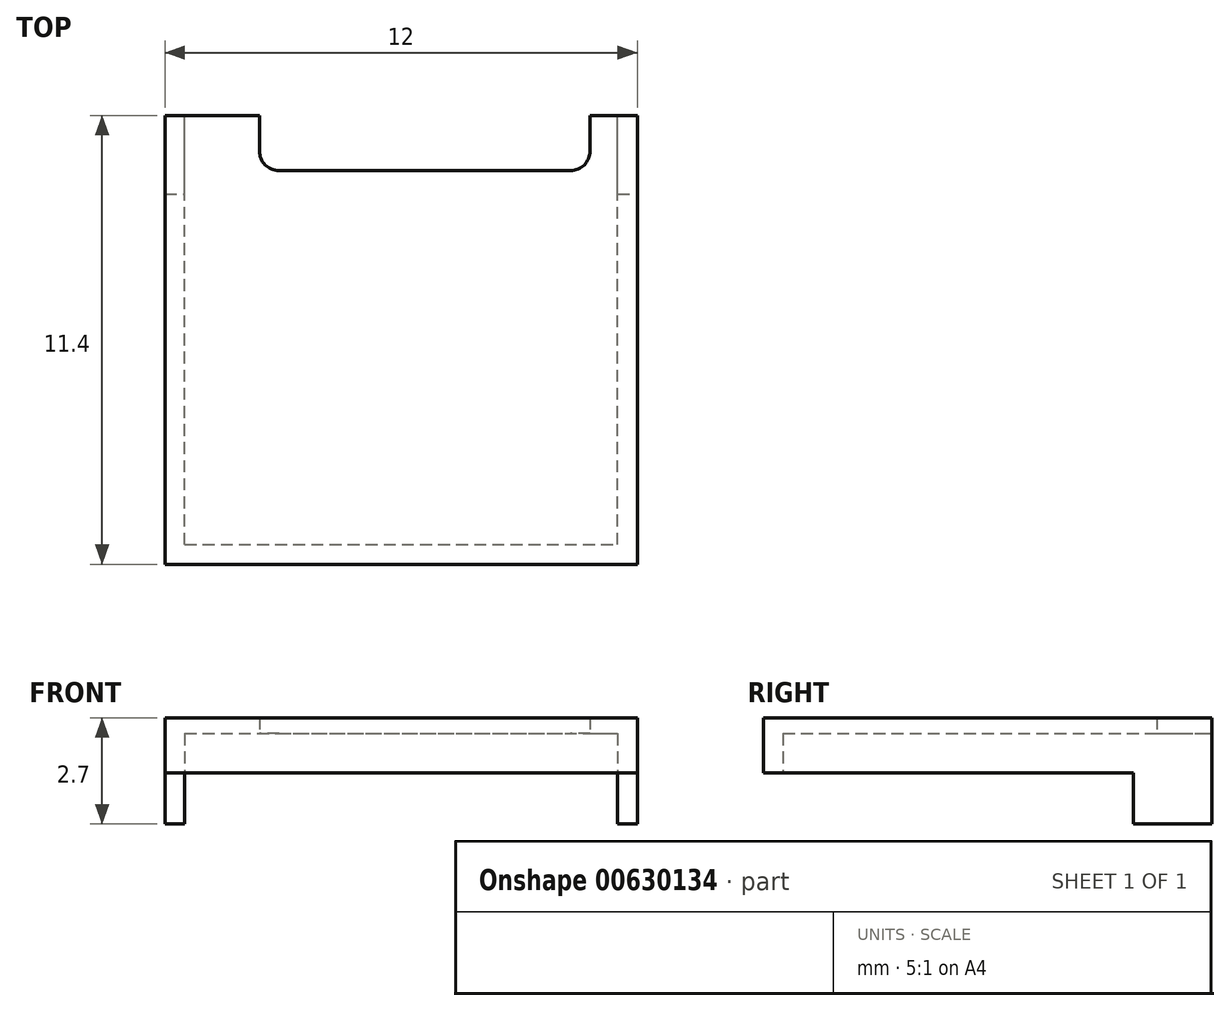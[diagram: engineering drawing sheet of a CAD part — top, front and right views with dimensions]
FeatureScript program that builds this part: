
annotation { "Feature Type Name" : "Feature", "Feature Type Description" : "" }
export const myFeature = defineFeature(function(context is Context, id is Id, definition is map)
    precondition{}
    {
        {
            var Q0;
            Q0=qCreatedBy(makeId("Top.planeOp"),FACE);
            var sketch = newSketch(context, id + "F0", { "sketchPlane" : qUnion([Q0])});
            skLineSegment(sketch, "E0.bottom", {"start": v(0, 0) * mm, "end": v(12, 0) * mm});
            skLineSegment(sketch, "E0.top", {"start": v(0, 11.4) * mm, "end": v(2.4, 11.4) * mm});
            skLineSegment(sketch, "E0.left", {"start": v(0, 0) * mm, "end": v(0, 11.4) * mm});
            skLineSegment(sketch, "E0.right", {"start": v(12, 0) * mm, "end": v(12, 11.4) * mm});
            skLineSegment(sketch, "E1", {"start": v(2.4, 11.4) * mm, "end": v(2.4, 10) * mm});
            skLineSegment(sketch, "E2", {"start": v(2.4, 10) * mm, "end": v(10.8, 10) * mm});
            skLineSegment(sketch, "E3", {"start": v(10.8, 10) * mm, "end": v(10.8, 11.4) * mm});
            skLineSegment(sketch, "E4.trimOffspring", {"start": v(10.8, 11.4) * mm, "end": v(12, 11.4) * mm});
            skSolve(sketch);
        }
        {
            var Q0;
            Q0=qSketchRegion(id+"F0",true);
            extrude(context, id + "F1", {"entities" : qUnion([Q0]), "depth" : 1.4 * mm});
        }
        {
            var Q0;
            Q0=makeQuery(id+"F1.opExtrude","CAP_FACE",FACE,{"disambiguationData":[OSD([sQuery(id+"F0.wireOp",EDGE,"E0.bottom"),sQuery(id+"F0.wireOp",EDGE,"E0.top"),sQuery(id+"F0.wireOp",EDGE,"E0.left"),sQuery(id+"F0.wireOp",EDGE,"E0.right"),sQuery(id+"F0.wireOp",EDGE,"E1"),sQuery(id+"F0.wireOp",EDGE,"E2"),sQuery(id+"F0.wireOp",EDGE,"E3"),sQuery(id+"F0.wireOp",EDGE,"E4.trimOffspring")])],"isStart":true});
            var sketch = newSketch(context, id + "F2", { "sketchPlane" : qUnion([Q0])});
            skLineSegment(sketch, "E5", {"start": v(0.5, -0.5) * mm, "end": v(11.5, -0.5) * mm});
            skLineSegment(sketch, "E6", {"start": v(11.5, -0.5) * mm, "end": v(11.5, -11.4) * mm});
            skLineSegment(sketch, "E7", {"start": v(0.5, -11.4) * mm, "end": v(2.4, -11.4) * mm});
            skLineSegment(sketch, "E8", {"start": v(2.4, -11.4) * mm, "end": v(2.4, -10) * mm});
            skLineSegment(sketch, "E9", {"start": v(2.4, -10) * mm, "end": v(10.8, -10) * mm});
            skLineSegment(sketch, "E10", {"start": v(10.8, -10) * mm, "end": v(10.8, -11.4) * mm});
            skLineSegment(sketch, "E11", {"start": v(10.8, -11.4) * mm, "end": v(11.5, -11.4) * mm});
            skLineSegment(sketch, "E12", {"start": v(0.5, -0.5) * mm, "end": v(0.5, -11.4) * mm});
            skSolve(sketch);
        }
        {
            var Q0;
            Q0=qSketchRegion(id+"F2",true);
            extrude(context, id + "F3", {"entities" : qUnion([Q0]), "operationType" : NewBodyOperationType.REMOVE, "oppositeDirection" : true, "depth" : 1 * mm});
        }
        {
            var Q0;
            Q0=makeQuery(id+"F1.opExtrude","CAP_FACE",FACE,{"disambiguationData":[OSD([sQuery(id+"F0.wireOp",EDGE,"E0.bottom"),sQuery(id+"F0.wireOp",EDGE,"E0.top"),sQuery(id+"F0.wireOp",EDGE,"E0.left"),sQuery(id+"F0.wireOp",EDGE,"E0.right"),sQuery(id+"F0.wireOp",EDGE,"E1"),sQuery(id+"F0.wireOp",EDGE,"E2"),sQuery(id+"F0.wireOp",EDGE,"E3"),sQuery(id+"F0.wireOp",EDGE,"E4.trimOffspring")])],"isStart":true});
            var sketch = newSketch(context, id + "F4", { "sketchPlane" : qUnion([Q0])});
            skLineSegment(sketch, "E13.bottom", {"start": v(0, -11.4) * mm, "end": v(0.5, -11.4) * mm});
            skLineSegment(sketch, "E13.top", {"start": v(0, -9.4) * mm, "end": v(0.5, -9.4) * mm});
            skLineSegment(sketch, "E13.left", {"start": v(0, -11.4) * mm, "end": v(0, -9.4) * mm});
            skLineSegment(sketch, "E13.right", {"start": v(0.5, -11.4) * mm, "end": v(0.5, -9.4) * mm});
            skLineSegment(sketch, "E14.bottom", {"start": v(11.5, -11.4) * mm, "end": v(12, -11.4) * mm});
            skLineSegment(sketch, "E14.top", {"start": v(11.5, -9.4) * mm, "end": v(12, -9.4) * mm});
            skLineSegment(sketch, "E14.left", {"start": v(11.5, -11.4) * mm, "end": v(11.5, -9.4) * mm});
            skLineSegment(sketch, "E14.right", {"start": v(12, -11.4) * mm, "end": v(12, -9.4) * mm});
            skSolve(sketch);
        }
        {
            var Q0;
            Q0=qSketchRegion(id+"F4",true);
            extrude(context, id + "F5", {"entities" : qUnion([Q0]), "operationType" : NewBodyOperationType.ADD, "depth" : 1.3 * mm});
        }
        {
            var Q0;
            Q0=makeQuery(id+"F1.opExtrude","SWEPT_EDGE",EDGE,{"disambiguationData":[OSD([sQuery(id+"F0.wireOp",EDGE,"E2"),sQuery(id+"F0.wireOp",EDGE,"E3")])]});
            var Q1;
            Q1=makeQuery(id+"F1.opExtrude","SWEPT_EDGE",EDGE,{"disambiguationData":[OSD([sQuery(id+"F0.wireOp",EDGE,"E1"),sQuery(id+"F0.wireOp",EDGE,"E2")])]});
            fillet(context, id + "F6", {"entities" : qUnion([Q0, Q1]), "radius" : 0.5 * mm, "tangentPropagation" : true, "allowEdgeOverflow" : false});
        }
    });
